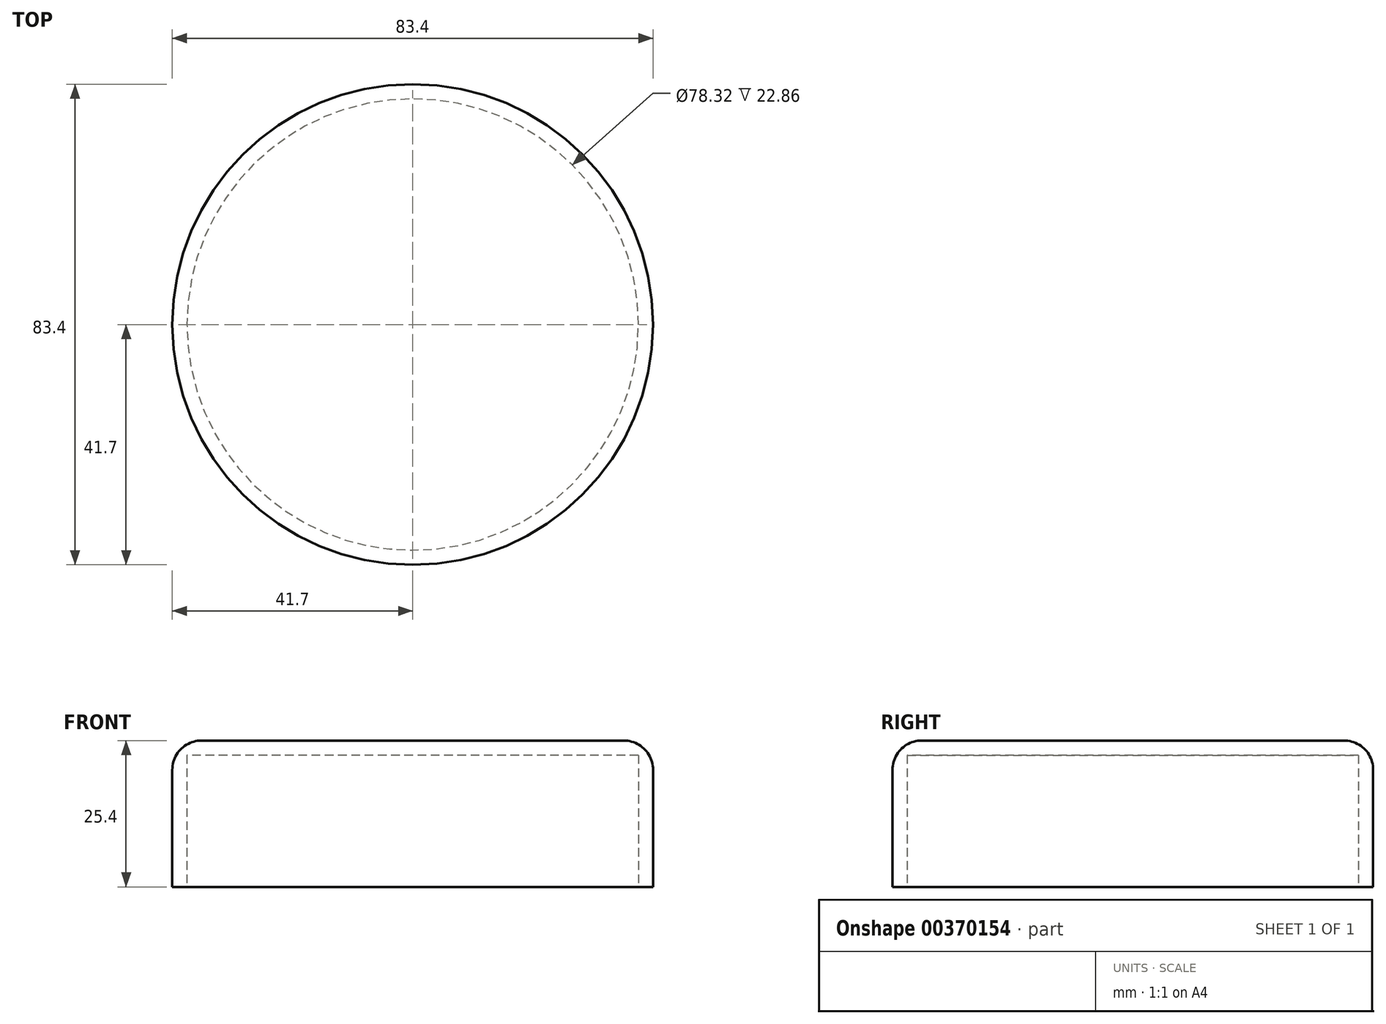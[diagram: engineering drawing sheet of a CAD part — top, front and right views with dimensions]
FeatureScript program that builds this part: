
annotation { "Feature Type Name" : "Feature", "Feature Type Description" : "" }
export const myFeature = defineFeature(function(context is Context, id is Id, definition is map)
    precondition{}
    {
        {
            var Q0;
            Q0=qCreatedBy(makeId("Top.planeOp"),FACE);
            var sketch = newSketch(context, id + "F0", { "sketchPlane" : qUnion([Q0])});
            skCircle(sketch, "E0", {"center": v(0, 0) * mm, "radius": 41.7 * mm});
            skSolve(sketch);
        }
        {
            var Q0;
            Q0=makeQuery(id+"F0.imprint","IMPRINT",FACE,{"disambiguationData":[TD([[makeQuery(id+"F0.imprint","IMPRINT",EDGE,{"derivedFrom":sQuery(id+"F0.wireOp",EDGE,"E0")}),1.0]])]});
            extrude(context, id + "F1", {"entities" : qUnion([Q0]), "depth" : 25.4 * mm});
        }
        {
            var Q0;
            Q0=makeQuery(id+"F1.opExtrude","CAP_FACE",FACE,{"disambiguationData":[OSD([sQuery(id+"F0.wireOp",EDGE,"E0")])],"isStart":true});
            shell(context, id + "F2", {"entities" : qUnion([Q0]), "thickness" : 2.54 * mm});
        }
        {
            var Q0;
            Q0=makeQuery(id+"F1.opExtrude","CAP_FACE",FACE,{"disambiguationData":[OSD([sQuery(id+"F0.wireOp",EDGE,"E0")])],"isStart":false});
            fillet(context, id + "F3", {"entities" : qUnion([Q0]), "radius" : 5.08 * mm, "tangentPropagation" : true, "allowEdgeOverflow" : false});
        }
    });
